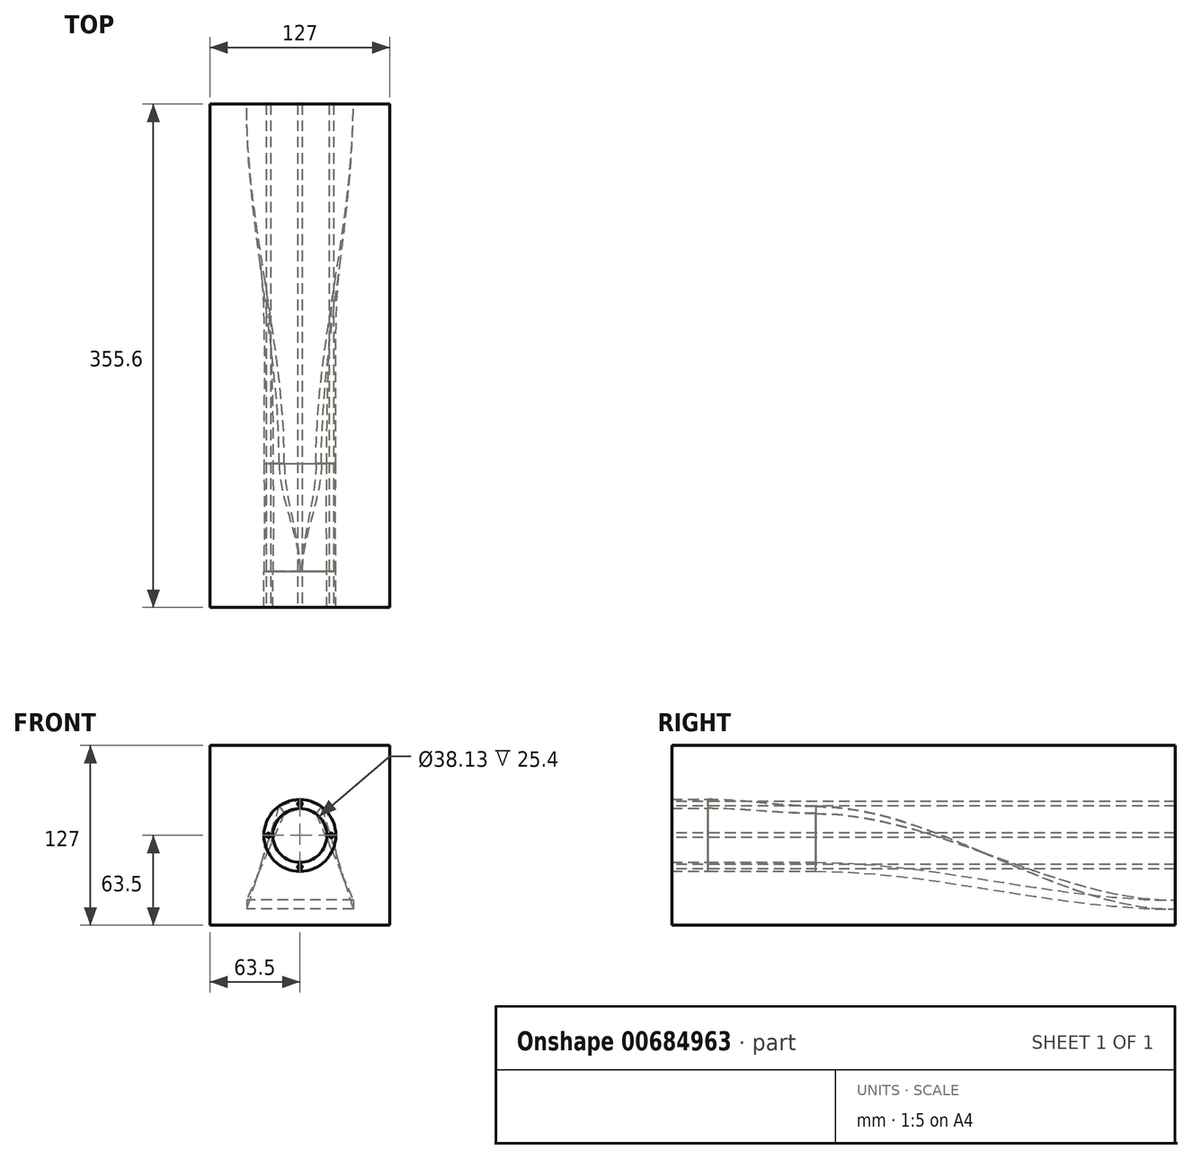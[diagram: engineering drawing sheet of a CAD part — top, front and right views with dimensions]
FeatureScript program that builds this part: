
annotation { "Feature Type Name" : "Feature", "Feature Type Description" : "" }
export const myFeature = defineFeature(function(context is Context, id is Id, definition is map)
    precondition{}
    {
        {
            var Q0;
            Q0=qCreatedBy(makeId("Front.planeOp"),FACE);
            var sketch = newSketch(context, id + "F0", { "sketchPlane" : qUnion([Q0])});
            skArc(sketch, "E0", {"start": v(-14.65, 20.75) * mm, "mid": v(-0.33, -25.4) * mm, "end": v(15.19, 20.36) * mm});
            skArc(sketch, "E1.0", {"start": v(-10.99, 15.56) * mm, "mid": v(-0.25, -19.05) * mm, "end": v(11.4, 15.27) * mm});
            skLineSegment(sketch, "E2", {"start": v(-14.65, 20.75) * mm, "end": v(-10.99, 15.56) * mm});
            skLineSegment(sketch, "E3", {"start": v(15.19, 20.36) * mm, "end": v(11.4, 15.27) * mm});
            skSolve(sketch);
        }
        {
            var Q0;
            Q0=qCreatedBy(makeId("Front.planeOp"),FACE);
            cPlane(context, id + "F1", {"entities" : qUnion([Q0]), "cplaneType" : CPlaneType.OFFSET, "offset" : 254 * mm, "oppositeDirection" : true, "width" : 152.4 * mm, "height" : 152.4 * mm});
        }
        {
            var Q0;
            Q0=qCreatedBy(id+"F1.planeOp",FACE);
            var sketch = newSketch(context, id + "F2", { "sketchPlane" : qUnion([Q0])});
            skLineSegment(sketch, "E4.bottom", {"start": v(37.65, -45.72) * mm, "end": v(-37.65, -45.72) * mm});
            skLineSegment(sketch, "E4.top", {"start": v(37.65, -52.07) * mm, "end": v(-37.65, -52.07) * mm});
            skLineSegment(sketch, "E4.left", {"start": v(37.65, -45.72) * mm, "end": v(37.65, -52.07) * mm});
            skLineSegment(sketch, "E4.right", {"start": v(-37.65, -45.72) * mm, "end": v(-37.65, -52.07) * mm});
            skPoint(sketch, "E4.middle", {"position": v(0, -48.9) * mm});
            skSolve(sketch);
        }
        {
            var Q0;
            Q0=makeQuery(id+"F0.imprint","IMPRINT",FACE,{"disambiguationData":[TD([[makeQuery(id+"F0.imprint","IMPRINT",EDGE,{"derivedFrom":sQuery(id+"F0.wireOp",EDGE,"E0")}),1.0]])]});
            var Q1;
            Q1=makeQuery(id+"F2.imprint","IMPRINT",FACE,{"disambiguationData":[TD([[makeQuery(id+"F2.imprint","IMPRINT",EDGE,{"derivedFrom":sQuery(id+"F2.wireOp",EDGE,"E4.bottom")}),1.0]])]});
            loft(context, id + "F3", {"startCondition" : LoftEndDerivativeType.NORMAL_TO_PROFILE, "startMagnitude" : 1, "endCondition" : LoftEndDerivativeType.NORMAL_TO_PROFILE, "endMagnitude" : 1, "sheetProfilesArray" : [{ "sheetProfileEntities" : qUnion([Q0]) }, { "sheetProfileEntities" : qUnion([Q1]) }]});
        }
        {
            var Q0;
            Q0=qCreatedBy(makeId("Front.planeOp"),FACE);
            cPlane(context, id + "F4", {"entities" : qUnion([Q0]), "cplaneType" : CPlaneType.OFFSET, "offset" : 76.2 * mm, "width" : 152.4 * mm, "height" : 152.4 * mm});
        }
        {
            var Q0;
            Q0=qCreatedBy(id+"F4.planeOp",FACE);
            var sketch = newSketch(context, id + "F5", { "sketchPlane" : qUnion([Q0])});
            skArc(sketch, "E5", {"start": v(0, 25.4) * mm, "mid": v(-0.76, -25.39) * mm, "end": v(1.51, 25.35) * mm});
            skArc(sketch, "E6.0", {"start": v(0, 19.05) * mm, "mid": v(-0.57, -19.04) * mm, "end": v(1.14, 19.02) * mm});
            skLineSegment(sketch, "E7", {"start": v(0, 25.4) * mm, "end": v(0, 19.05) * mm});
            skLineSegment(sketch, "E8", {"start": v(1.51, 25.35) * mm, "end": v(1.14, 19.02) * mm});
            skSolve(sketch);
        }
        {
            var Q1;
            Q1=makeQuery(id+"F3.opLoft","CAP_FACE",FACE,{"disambiguationData":[OSD([makeQuery(id+"F0.imprint","IMPRINT",FACE,{"disambiguationData":[TD([[makeQuery(id+"F0.imprint","IMPRINT",EDGE,{"derivedFrom":sQuery(id+"F0.wireOp",EDGE,"E0")}),1.0]])]})])],"isStart":true});
            var Q2;
            Q2=makeQuery(id+"F5.imprint","IMPRINT",FACE,{"disambiguationData":[TD([[makeQuery(id+"F5.imprint","IMPRINT",EDGE,{"derivedFrom":sQuery(id+"F5.wireOp",EDGE,"E5")}),1.0]])]});
            loft(context, id + "F6", {"startCondition" : LoftEndDerivativeType.NORMAL_TO_PROFILE, "startMagnitude" : 1, "endCondition" : LoftEndDerivativeType.NORMAL_TO_PROFILE, "endMagnitude" : 1, "sheetProfilesArray" : [{ "sheetProfileEntities" : qUnion([Q1]) }, { "sheetProfileEntities" : qUnion([Q2]) }]});
        }
        {
            var Q0;
            Q0=qCreatedBy(id+"F4.planeOp",FACE);
            var sketch = newSketch(context, id + "F7", { "sketchPlane" : qUnion([Q0])});
            skCircle(sketch, "E9", {"center": v(0, 0) * mm, "radius": 25.42 * mm});
            skCircle(sketch, "E10.0", {"center": v(0, 0) * mm, "radius": 19.07 * mm});
            skSolve(sketch);
        }
        {
            var Q0;
            Q0=makeQuery(id+"F7.imprint","IMPRINT",FACE,{"disambiguationData":[TD([[makeQuery(id+"F7.imprint","IMPRINT",EDGE,{"derivedFrom":sQuery(id+"F7.wireOp",EDGE,"E9")}),1.0]])]});
            extrude(context, id + "F8", {"entities" : qUnion([Q0]), "operationType" : NewBodyOperationType.ADD, "depth" : 25.4 * mm});
        }
        {
            var Q0;
            Q0=qCreatedBy(id+"F4.planeOp",FACE);
            cPlane(context, id + "F9", {"entities" : qUnion([Q0]), "cplaneType" : CPlaneType.OFFSET, "offset" : 25.4 * mm, "width" : 152.4 * mm, "height" : 152.4 * mm});
        }
        {
            var Q0;
            Q0=qCreatedBy(id+"F9.planeOp",FACE);
            var sketch = newSketch(context, id + "F10", { "sketchPlane" : qUnion([Q0])});
            skLineSegment(sketch, "E11.bottom", {"start": v(-63.5, 63.5) * mm, "end": v(63.5, 63.5) * mm});
            skLineSegment(sketch, "E11.top", {"start": v(-63.5, -63.5) * mm, "end": v(63.5, -63.5) * mm});
            skLineSegment(sketch, "E11.left", {"start": v(-63.5, 63.5) * mm, "end": v(-63.5, -63.5) * mm});
            skLineSegment(sketch, "E11.right", {"start": v(63.5, 63.5) * mm, "end": v(63.5, -63.5) * mm});
            skPoint(sketch, "E11.middle", {"position": v(0, 0) * mm});
            skSolve(sketch);
        }
        {
            var Q0;
            Q0=makeQuery(id+"F10.imprint","IMPRINT",FACE,{"disambiguationData":[TD([[makeQuery(id+"F10.imprint","IMPRINT",EDGE,{"derivedFrom":sQuery(id+"F10.wireOp",EDGE,"E11.bottom")}),-1.0]])]});
            extrude(context, id + "F11", {"entities" : qUnion([Q0]), "oppositeDirection" : true, "depth" : 355.6 * mm});
        }
        {
            var Q0;
            Q0=qCreatedBy(id+"F9.planeOp",FACE);
            var sketch = newSketch(context, id + "F12", { "sketchPlane" : qUnion([Q0])});
            skCircle(sketch, "E12", {"center": v(0.01, 22.24) * mm, "radius": 1.59 * mm});
            skCircle(sketch, "E13", {"center": v(-22.21, 0.02) * mm, "radius": 1.59 * mm});
            skCircle(sketch, "E14", {"center": v(22.24, -0.01) * mm, "radius": 1.59 * mm});
            skCircle(sketch, "E15", {"center": v(0.01, -22.24) * mm, "radius": 1.59 * mm});
            skSolve(sketch);
        }
        {
            var Q0;
            Q0=qSketchRegion(id+"F12",true);
            extrude(context, id + "F13", {"entities" : qUnion([Q0]), "oppositeDirection" : true, "depth" : 355.6 * mm});
        }
    });
